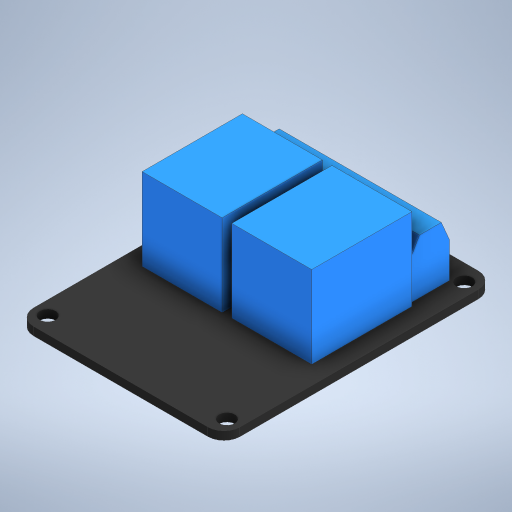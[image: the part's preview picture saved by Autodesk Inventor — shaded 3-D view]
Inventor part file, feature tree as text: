
AUTODESK INVENTOR PART (.ipt)
format: ipt  version: 2023.1 (Build 271208000, 208)  size: 299,008 bytes
history: native  units: mm
features: sketch x4, extrude x3, other x1
ambient origin geometry x8: Origin, YZ Plane, XZ Plane, XY Plane, X Axis, Y Axis, Z Axis, Center Point
bodies: Body1 (feature_tree)
feature tree (8):
  other  "솔리드1"
  sketch  "스케치1"
  extrude  "돌출1"  Depth=38.7mm
  extrude  "돌출2"  Depth=50.7mm
  extrude  "돌출3"  Depth=3.0mm
  sketch  "스케치2"
  sketch  "스케치3"
  sketch  "스케치4"
